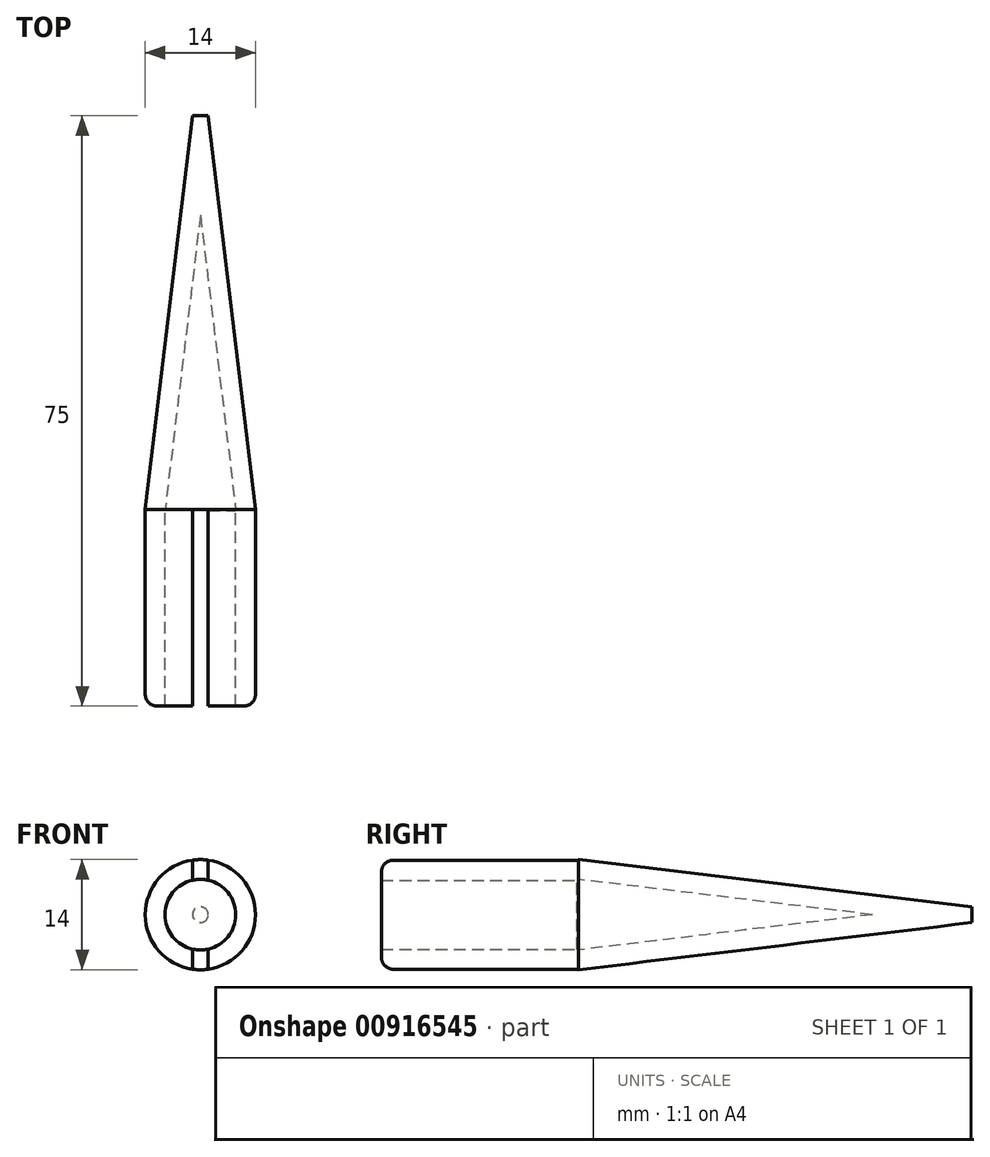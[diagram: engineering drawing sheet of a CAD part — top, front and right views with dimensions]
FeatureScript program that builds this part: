
annotation { "Feature Type Name" : "Feature", "Feature Type Description" : "" }
export const myFeature = defineFeature(function(context is Context, id is Id, definition is map)
    precondition{}
    {
        {
            var Q0;
            Q0=qCreatedBy(makeId("Front.planeOp"),FACE);
            var sketch = newSketch(context, id + "F0", { "sketchPlane" : qUnion([Q0])});
            skCircle(sketch, "E0", {"center": v(0, 0) * mm, "radius": 7 * mm});
            skSolve(sketch);
        }
        {
            var Q0;
            Q0 = qSketchRegion(id + "F0", true);
            extrude(context, id + "F1", {"entities" : qUnion([Q0]), "depth" : 25 * mm, "offsetDistance" : 25 * mm});
        }
        {
            var Q0;
            Q0=qCreatedBy(makeId("Front.planeOp"),FACE);
            cPlane(context, id + "F2", {"entities" : qUnion([Q0]), "cplaneType" : CPlaneType.OFFSET, "offset" : 50 * mm, "oppositeDirection" : true, "width" : 150 * mm, "height" : 150 * mm});
        }
        {
            var Q0;
            Q0=qCreatedBy(id+"F2.planeOp",FACE);
            var sketch = newSketch(context, id + "F3", { "sketchPlane" : qUnion([Q0])});
            skCircle(sketch, "E1", {"center": v(0, 0) * mm, "radius": 1 * mm});
            skSolve(sketch);
        }
        {
            var Q1;
            Q1=makeQuery(id+"F3.imprint","IMPRINT",FACE,{"disambiguationData":[TD([[makeQuery(id+"F3.imprint","IMPRINT",EDGE,{"derivedFrom":sQuery(id+"F3.wireOp",EDGE,"E1")}),1.0]])]});
            var Q2;
            Q2=makeQuery(id+"F1.opExtrude","CAP_FACE",FACE,{"disambiguationData":[OSD([sQuery(id+"F0.wireOp",EDGE,"E0")])],"isStart":true});
            loft(context, id + "F4", {"operationType" : NewBodyOperationType.ADD, "sheetProfilesArray" : [{ "sheetProfileEntities" : qUnion([Q1]) }, { "sheetProfileEntities" : qUnion([Q2]) }]});
        }
        {
            var Q0;
            Q0=makeQuery(id+"F1.opExtrude","CAP_FACE",FACE,{"disambiguationData":[OSD([sQuery(id+"F0.wireOp",EDGE,"E0")])],"isStart":false});
            var Q1;
            Q1=makeQuery(id+"F6.opFillet","BLEND_FACE",FACE,{"disambiguationData":[OSD([sQuery(id+"F0.wireOp",EDGE,"E0")])]});
            shell(context, id + "F5", {"entities" : qUnion([Q0, Q1]), "thickness" : 2.5 * mm});
        }
        {
            var Q0;
            Q0=makeQuery(id+"F1.opExtrude","CAP_EDGE",EDGE,{"disambiguationData":[OSD([sQuery(id+"F0.wireOp",EDGE,"E0")])],"isStart":false});
            fillet(context, id + "F6", {"entities" : qUnion([Q0]), "radius" : 1.5 * mm, "tangentPropagation" : true, "allowEdgeOverflow" : false});
        }
        {
            var Q0;
            Q0=qCreatedBy(makeId("Front.planeOp"),FACE);
            cPlane(context, id + "F7", {"entities" : qUnion([Q0]), "cplaneType" : CPlaneType.OFFSET, "offset" : 25 * mm, "width" : 150 * mm, "height" : 150 * mm});
        }
        {
            var Q0;
            Q0=qCreatedBy(id+"F7.planeOp",FACE);
            var sketch = newSketch(context, id + "F8", { "sketchPlane" : qUnion([Q0])});
            skLineSegment(sketch, "E2.bottom", {"start": v(1, 10.75) * mm, "end": v(-1, 10.75) * mm});
            skLineSegment(sketch, "E2.top", {"start": v(1, -10.75) * mm, "end": v(-1, -10.75) * mm});
            skLineSegment(sketch, "E2.left", {"start": v(1, 10.75) * mm, "end": v(1, -10.75) * mm});
            skLineSegment(sketch, "E2.right", {"start": v(-1, 10.75) * mm, "end": v(-1, -10.75) * mm});
            skPoint(sketch, "E2.middle", {"position": v(0, 0) * mm});
            skSolve(sketch);
        }
        {
            var Q0;
            Q0=makeQuery(id+"F8.imprint","IMPRINT",FACE,{"disambiguationData":[TD([[makeQuery(id+"F8.imprint","IMPRINT",EDGE,{"derivedFrom":sQuery(id+"F8.wireOp",EDGE,"E2.bottom")}),1.0]])]});
            extrude(context, id + "F9", {"entities" : qUnion([Q0]), "operationType" : NewBodyOperationType.REMOVE, "oppositeDirection" : true, "depth" : 25 * mm, "offsetDistance" : 25 * mm});
        }
    });
